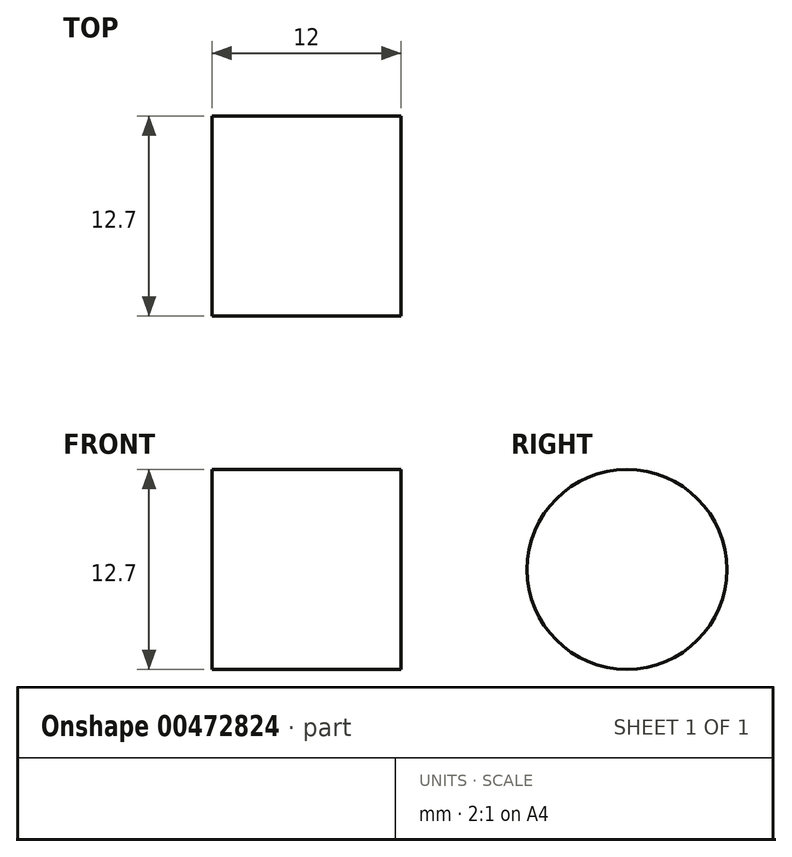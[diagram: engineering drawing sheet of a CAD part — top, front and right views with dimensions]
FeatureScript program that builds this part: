
annotation { "Feature Type Name" : "Feature", "Feature Type Description" : "" }
export const myFeature = defineFeature(function(context is Context, id is Id, definition is map)
    precondition{}
    {
        {
            assignVariable(context, id + "F0", {"name" : "ShaftLength", "anyValue" : 12});
        }
        {
            var Q0;
            Q0=qCreatedBy(makeId("Right.planeOp"),FACE);
            var sketch = newSketch(context, id + "F1", { "sketchPlane" : qUnion([Q0])});
            skCircle(sketch, "E0", {"center": v(0, 0) * mm, "radius": 6.35 * mm});
            skSolve(sketch);
        }
        {
            var Q0;
            Q0=makeQuery(id+"F1.imprint","IMPRINT",FACE,{"disambiguationData":[TD([[makeQuery(id+"F1.imprint","IMPRINT",EDGE,{"derivedFrom":sQuery(id+"F1.wireOp",EDGE,"E0")}),1.0]])]});
            extrude(context, id + "F2", {"entities" : qUnion([Q0]), "depth" : (getVariable(context, 'ShaftLength')) * mm});
        }
    });
